# Revit family: 50-520-1-160
name_source: partatom
category: Sprinklers
revit_build: Autodesk Revit 2016 (Build: 20150220_1215(x64)
units: mm (PartAtom-declared; Revit-internal decimal feet)

## family parameters
Always vertical = Yes
Cut with Voids When Loaded = No
Maintain Annotation Orientation = No
OmniClass Number = 23.65.70.17.11.24
OmniClass Title = Fire Fighting Sprinkler Heads
Part Type = Normal
Room Calculation Point = No
Round Connector Dimension = Use Diameter
Shared = No
Work Plane-Based = No

## types (1)
- Tyco LFII Sidewall K4.2/60 160°F/71°C ½"/DN15 NPT Brass TY2324_50-520-1-160
    COBie = Yes
    COBie.Component.Description = ½"/DN15 Tyco LFII Wet Horizontal Sidewall 160°F/71°C  K4.2/60  NPT Br
    COBie.Component.Name = Sprinklers:Concealed Flush
    COBie.Type = Yes
    COBie.Type.AssetType = Fixed
    COBie.Type.Category = Pr_70_55_97_84:Sprinklers
    COBie.Type.DurationUnit = year
    COBie.Type.Finish = Brass
    COBie.Type.Manufacturer = Tyco Fire Protection Products
    COBie.Type.Material = Brass
    COBie.Type.ModelNumber = 50-520-1-160
    COBie.Type.ModelReference = ½"/DN15 Tyco LFII Wet Horizontal Sidewall 160°F/71°C  K4.2/60  NPT Br
    COBie.Type.NominalHeight = 0' - 0"
    COBie.Type.NominalLength = 0' - 0"
    COBie.Type.NominalWidth = 0' - 0"
    COBie.Type.ReplacementCost = 0 $
    COBie.Type.Shape = Cylinder
    COBie.Type.Size = 1/2"(DN15)
    COBie.Type.WarrantyGuarantorParts = http://tycofsbp.com
    Coverage = Standard
    Description = Tyco LFII Sidewall K4.2/60 160°F/71°C ½"/DN15 NPT Brass TY2324_50-520-1-160
    K-Factor = 4.162
    Manufacturer = Tyco Fire Protection Products
    Manufacturer URL = www.tyco-fire.com
    Model = LFII
    Nominal Diameter 1 = 1"
    Orifice = Standard
    Orifice Size = 0"
    Outside Diameter 1 = 1"
    Part No = 50-520-1-160
    Style Id = 0
    Takeout 1 = 2"
    Technical Data Sheet No = TFP445
    Temperature Rating = 160 °F

## geometry (parser evidence)
native form markers: Blend x4, Sweep x32
no freeform markers — native parametric forms only
